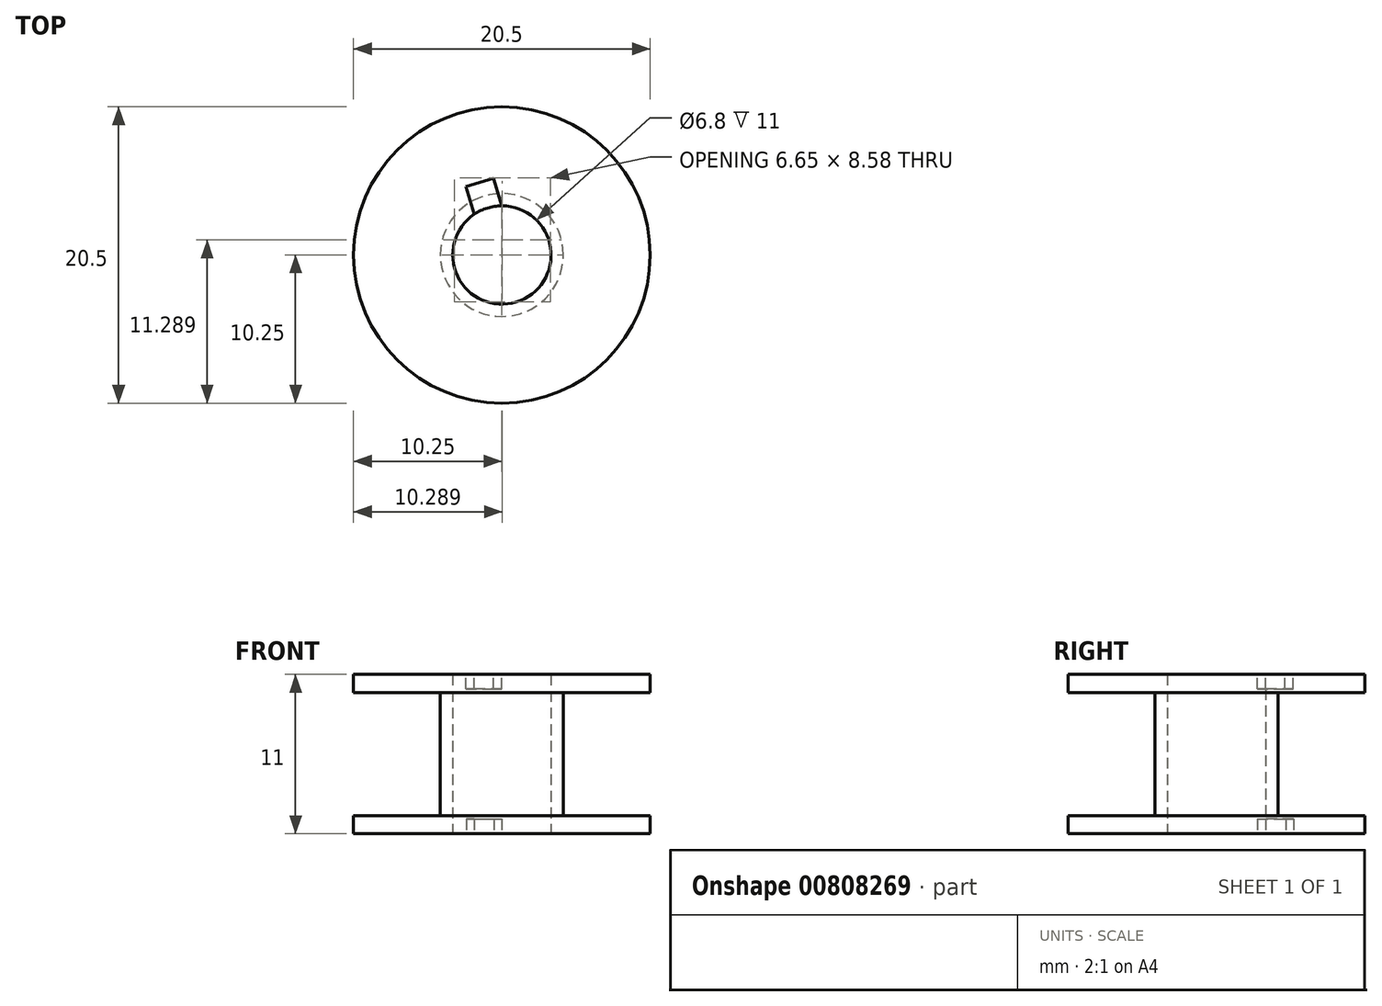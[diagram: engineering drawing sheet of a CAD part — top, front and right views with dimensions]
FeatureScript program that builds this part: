
annotation { "Feature Type Name" : "Feature", "Feature Type Description" : "" }
export const myFeature = defineFeature(function(context is Context, id is Id, definition is map)
    precondition{}
    {
        {
            var Q0;
            Q0=qCreatedBy(makeId("Top.planeOp"),FACE);
            var sketch = newSketch(context, id + "F0", { "sketchPlane" : qUnion([Q0])});
            skCircle(sketch, "E0", {"center": v(0, 0) * mm, "radius": 3.4 * mm});
            skCircle(sketch, "E1", {"center": v(0, 0) * mm, "radius": 10.25 * mm});
            skCircle(sketch, "E2", {"center": v(0, 0) * mm, "radius": 4.9 * mm});
            skSolve(sketch);
        }
        {
            var Q0;
            Q0 = qSketchRegion(id + "F0", true);
            var Q1;
            Q1=makeQuery(id+"F0.imprint","IMPRINT",FACE,{"disambiguationData":[TD([[makeQuery(id+"F0.imprint","IMPRINT",EDGE,{"derivedFrom":sQuery(id+"F0.wireOp",EDGE,"E0")}),-1.0]])]});
            extrude(context, id + "F1", {"entities" : qUnion([Q0, Q1]), "endBound" : BoundingType.SYMMETRIC, "depth" : 11 * mm, "offsetDistance" : 25 * mm});
        }
        {
            var Q0;
            Q0=qCreatedBy(makeId("Top.planeOp"),FACE);
            var sketch = newSketch(context, id + "F2", { "sketchPlane" : qUnion([Q0])});
            skCircle(sketch, "E3", {"center": v(0, 0) * mm, "radius": 4.25 * mm});
            skCircle(sketch, "E4", {"center": v(0, 0) * mm, "radius": 10.25 * mm});
            skSolve(sketch);
        }
        {
            var Q0;
            Q0 = qSketchRegion(id + "F2", true);
            extrude(context, id + "F3", {"entities" : qUnion([Q0]), "operationType" : NewBodyOperationType.REMOVE, "endBound" : BoundingType.SYMMETRIC, "oppositeDirection" : true, "depth" : 8.5 * mm, "offsetDistance" : 25 * mm});
        }
        {
            var Q0;
            Q0=makeQuery(id+"F1.opExtrude","CAP_FACE",FACE,{"disambiguationData":[OSD([sQuery(id+"F0.wireOp",EDGE,"E0"),sQuery(id+"F0.wireOp",EDGE,"E1")])],"isStart":false});
            var sketch = newSketch(context, id + "F4", { "sketchPlane" : qUnion([Q0])});
            skArc(sketch, "E5", {"start": v(0, 3.4) * mm, "mid": v(-1, 3.25) * mm, "end": v(-1.91, 2.81) * mm});
            skLineSegment(sketch, "E6", {"start": v(-1.91, 2.81) * mm, "end": v(-2.5, 4.72) * mm});
            skLineSegment(sketch, "E7", {"start": v(-2.5, 4.72) * mm, "end": v(-0.59, 5.31) * mm});
            skLineSegment(sketch, "E8", {"start": v(-0.59, 5.31) * mm, "end": v(0, 3.4) * mm});
            skSolve(sketch);
        }
        {
            var Q0;
            Q0 = qSketchRegion(id + "F4", true);
            extrude(context, id + "F5", {"entities" : qUnion([Q0]), "operationType" : NewBodyOperationType.REMOVE, "oppositeDirection" : true, "depth" : 1 * mm, "offsetDistance" : 25 * mm});
        }
        {
            var Q0;
            Q0=makeQuery(id+"F1.opExtrude","CAP_FACE",FACE,{"disambiguationData":[OSD([sQuery(id+"F0.wireOp",EDGE,"E0"),sQuery(id+"F0.wireOp",EDGE,"E1")])],"isStart":true});
            var sketch = newSketch(context, id + "F6", { "sketchPlane" : qUnion([Q0])});
            skArc(sketch, "E9", {"start": v(-1.91, -2.81) * mm, "mid": v(-1, -3.22) * mm, "end": v(0, -3.4) * mm});
            skLineSegment(sketch, "E10", {"start": v(-1.91, -2.81) * mm, "end": v(-2.46, -4.79) * mm});
            skLineSegment(sketch, "E11", {"start": v(-2.46, -4.79) * mm, "end": v(-0.54, -5.33) * mm});
            skLineSegment(sketch, "E12", {"start": v(-0.54, -5.33) * mm, "end": v(0, -3.4) * mm});
            skSolve(sketch);
        }
        {
            var Q0;
            Q0 = qSketchRegion(id + "F6", true);
            extrude(context, id + "F7", {"entities" : qUnion([Q0]), "operationType" : NewBodyOperationType.REMOVE, "oppositeDirection" : true, "depth" : 1 * mm, "offsetDistance" : 25 * mm});
        }
    });
